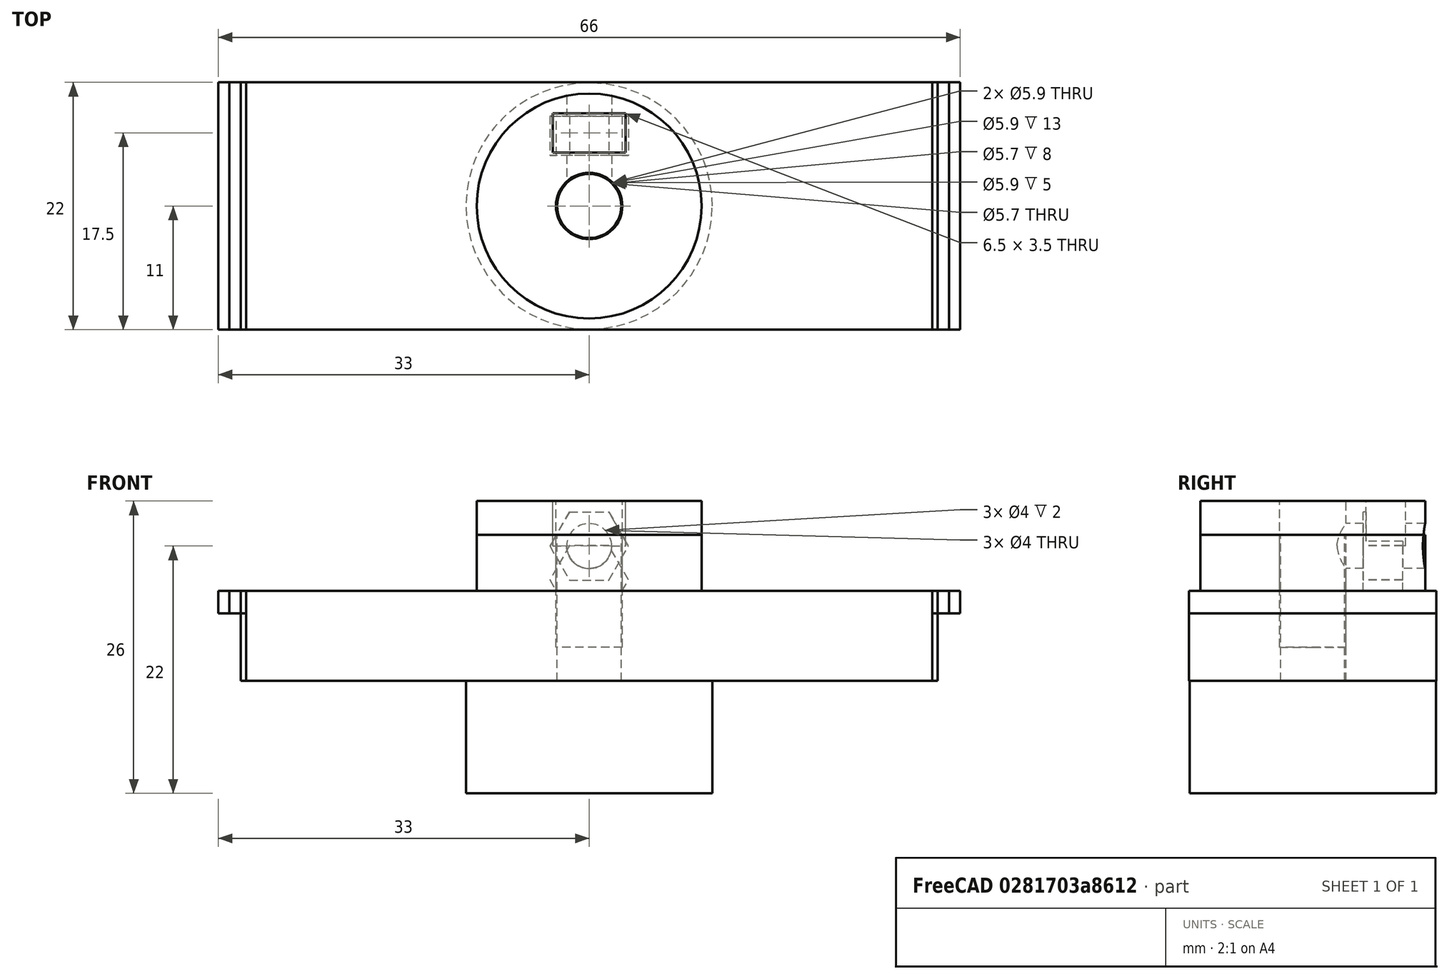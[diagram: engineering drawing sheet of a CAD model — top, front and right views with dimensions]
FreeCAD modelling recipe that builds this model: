
FCSTD DOCUMENT  (FreeCAD 0.18R4 (GitTag))
Label: Soporte bobina-eje
License: All rights reserved
LicenseURL: http://en.wikipedia.org/wiki/All_rights_reserved
objects: Part::Cut×8, Part::Cylinder×7, Part::MultiFuse×5, Part::Box×4, Part::Feature×3, Part::Prism×2
note: 29 computed .brp shape members not serialized (recipe doc carries the construction recipe); baked Part::Feature solids carry a one-line shape summary decoded from their .brp

FEATURE [Part::Box] Box002  label="Cubo002"
  AttacherType = Attacher::AttachEngine3D
  Height = 22
  Length = 62
  Placement = pos=(-31,11,0) rot=(1,0,0;1.5708rad)
  Width = 8
FEATURE [Part::Cylinder] Cylinder005  label="Cilindro005"
  Angle = 360
  AttacherType = Attacher::AttachEngine3D
  Height = 13
  Radius = 10
FEATURE [Part::Cylinder] Cylinder006  label="Cilindro006"
  Angle = 360
  AttacherType = Attacher::AttachEngine3D
  Height = 25
  Placement = pos=(0,0,-7) rot=(0,0,1;0rad)
  Radius = 2.95
FEATURE [Part::Cut] Cut005
  Base = -> Cylinder005
  Tool = -> Cylinder006
FEATURE [Part::Prism] Prism001  label="Prisma001"
  AttacherType = Attacher::AttachEngine3D
  Circumradius = 3.5
  Height = 3.5
  Placement = pos=(0,8,9) rot=(1,0,0;1.5708rad)
  Polygon = 6
FEATURE [Part::Cut] Cut006
  Base = -> Cut005
  Tool = -> Prism001
FEATURE [Part::Cylinder] Cylinder007  label="Cilindro007"
  Angle = 360
  AttacherType = Attacher::AttachEngine3D
  Height = 25
  Placement = pos=(0,0,-7) rot=(0,0,1;0rad)
  Radius = 2.85
FEATURE [Part::Cut] Cut
  Base = -> Box002
  Tool = -> Cylinder007
FEATURE [Part::MultiFuse] Fusion
  Shapes = -> [Cut,Cut006]
FEATURE [Part::Feature] Fusion001
  shape: bbox 61 x 22 x 13 mm, 17 faces (baked)
FEATURE [Part::Box] Box  label="Cubo"
  AttacherType = Attacher::AttachEngine3D
  Height = 2
  Length = 5
  Placement = pos=(-33,-11,6) rot=(0,0,1;0rad)
  Width = 22
FEATURE [Part::Box] Box003  label="Cubo003"
  AttacherType = Attacher::AttachEngine3D
  Height = 2
  Length = 5
  Placement = pos=(28,-11,6) rot=(0,0,1;0rad)
  Width = 22
FEATURE [Part::Cylinder] Cylinder008  label="Cilindro008"
  Angle = 360
  AttacherType = Attacher::AttachEngine3D
  Height = 13
  Radius = 10
FEATURE [Part::Cylinder] Cylinder009  label="Cilindro009"
  Angle = 360
  AttacherType = Attacher::AttachEngine3D
  Height = 25
  Placement = pos=(0,0,-7) rot=(0,0,1;0rad)
  Radius = 2.85
FEATURE [Part::Cut] Cut007
  Base = -> Cylinder008
  Tool = -> Cylinder009
FEATURE [Part::Prism] Prism002  label="Prisma002"
  AttacherType = Attacher::AttachEngine3D
  Circumradius = 3.5
  Height = 3.5
  Placement = pos=(0,8,9) rot=(1,0,0;1.5708rad)
  Polygon = 6
FEATURE [Part::Cut] Cut008
  Base = -> Cut007
  Tool = -> Prism002
FEATURE [Part::Box] Box004  label="Cubo004"
  AttacherType = Attacher::AttachEngine3D
  Height = 6.5
  Length = 6.5
  Placement = pos=(-3.25,4.75,9) rot=(0,0,1;0rad)
  Width = 3.5
FEATURE [Part::Cut] Cut009
  Base = -> Cut008
  Tool = -> Box004
FEATURE [Part::Cylinder] Cylinder010  label="Cilindro010"
  Angle = 360
  AttacherType = Attacher::AttachEngine3D
  Height = 10
  Placement = pos=(0,11,9) rot=(1,0,0;1.5708rad)
  Radius = 2
FEATURE [Part::Cut] Cut010
  Base = -> Cut009
  Placement = pos=(0,0,3) rot=(0,0,1;0rad)
  Tool = -> Cylinder010
FEATURE [Part::MultiFuse] Fusion002
  Shapes = -> [Cut010,Cut]
FEATURE [Part::Cut] Cut011
  Base = -> Fusion002
  Tool = -> Cylinder006
FEATURE [Part::MultiFuse] Fusion003
  Shapes = -> [Cut011,Box]
FEATURE [Part::MultiFuse] Fusion004
  Shapes = -> [Fusion003,Box003]
FEATURE [Part::Feature] Fusion004001  label="Soporte bobina-eje"
  shape: bbox 64 x 22 x 16 mm, 29 faces (baked)
FEATURE [Part::Feature] Fusion004002  label="Soporte bobina-eje 2"
  shape: bbox 66 x 22 x 16 mm, 29 faces (baked)
FEATURE [Part::Cylinder] Cylinder011  label="Cilindro011"
  Angle = 360
  AttacherType = Attacher::AttachEngine3D
  Height = 13
  Placement = pos=(0,0,-10) rot=(0,0,1;0rad)
  Radius = 10.95
FEATURE [Part::MultiFuse] Fusion004003  label="Soporte bobina-eje 3"
  Shapes = -> [Cylinder011,Fusion004]
